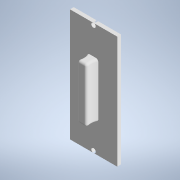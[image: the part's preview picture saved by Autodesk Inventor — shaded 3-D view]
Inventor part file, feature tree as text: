
AUTODESK INVENTOR PART (.ipt)
format: ipt  version: 2022 (Build 260153000, 153)  size: 166,400 bytes
history: native  units: mm
features: reference x6, other x4, extrude x3, sketch x3, fillet x2, projected_geometry x1
ambient origin geometry x8: Origin, YZ Plane, XZ Plane, XY Plane, X Axis, Y Axis, Z Axis, Center Point
bodies: Body1 (feature_tree)
feature tree (19):
  other  "Твердое тело1"
  extrude  "Выдавливание1"  Depth=0.3mm
  extrude  "Выдавливание2"  Depth=0.3mm
  extrude  "Выдавливание3"  Depth=0.3mm
  fillet  "Сопряжение1"  Radius=0.3mm
  fillet  "Сопряжение2"  Radius=3.5mm
  sketch  "Эскиз1"
  reference  "Ссылка1"
  reference  "Ссылка2"
  reference  "Ссылка3"
  reference  "Ссылка4"
  reference  "Ссылка5"
  reference  "Ссылка6"
  sketch  "Эскиз2"
  projected_geometry  "Спроецированная петля1"
  sketch  "Эскиз3"
  other  "<path> - Robot.iam"
  other  "000.000 - Robot.iam"
  other  "battery_case:1"
note: 1 file-system path scrubbed to <path> (originals preserved in map.json)
